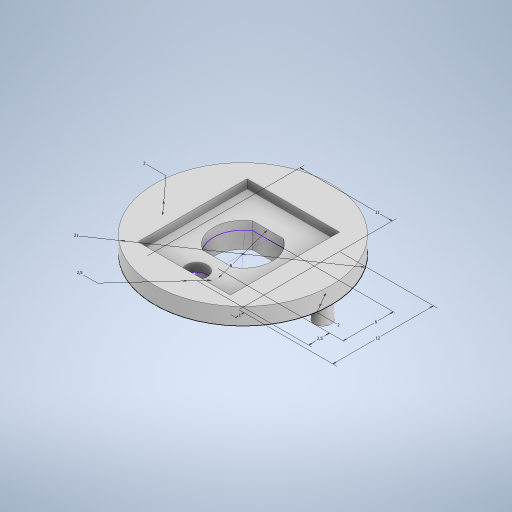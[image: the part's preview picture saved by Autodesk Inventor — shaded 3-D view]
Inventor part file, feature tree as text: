
AUTODESK INVENTOR PART (.ipt)
format: ipt  version: 2024 (Build 280153000, 153)  size: 292,864 bytes
history: native  units: mm
features: extrude x5, other x1, sketch x1
ambient origin geometry x8: Origin, YZ Plane, XZ Plane, XY Plane, X Axis, Y Axis, Z Axis, Center Point
bodies: Body1 (feature_tree)
feature tree (7):
  other  "Твердое тело1"
  sketch  "Эскиз1"
  extrude  "Выдавливание1"  Depth=21.0mm
  extrude  "Выдавливание2"  Depth=8.0mm
  extrude  "Выдавливание3"  Depth=7.0mm
  extrude  "Выдавливание4"  Depth=6.0mm
  extrude  "Выдавливание5"  Depth=2.5mm
